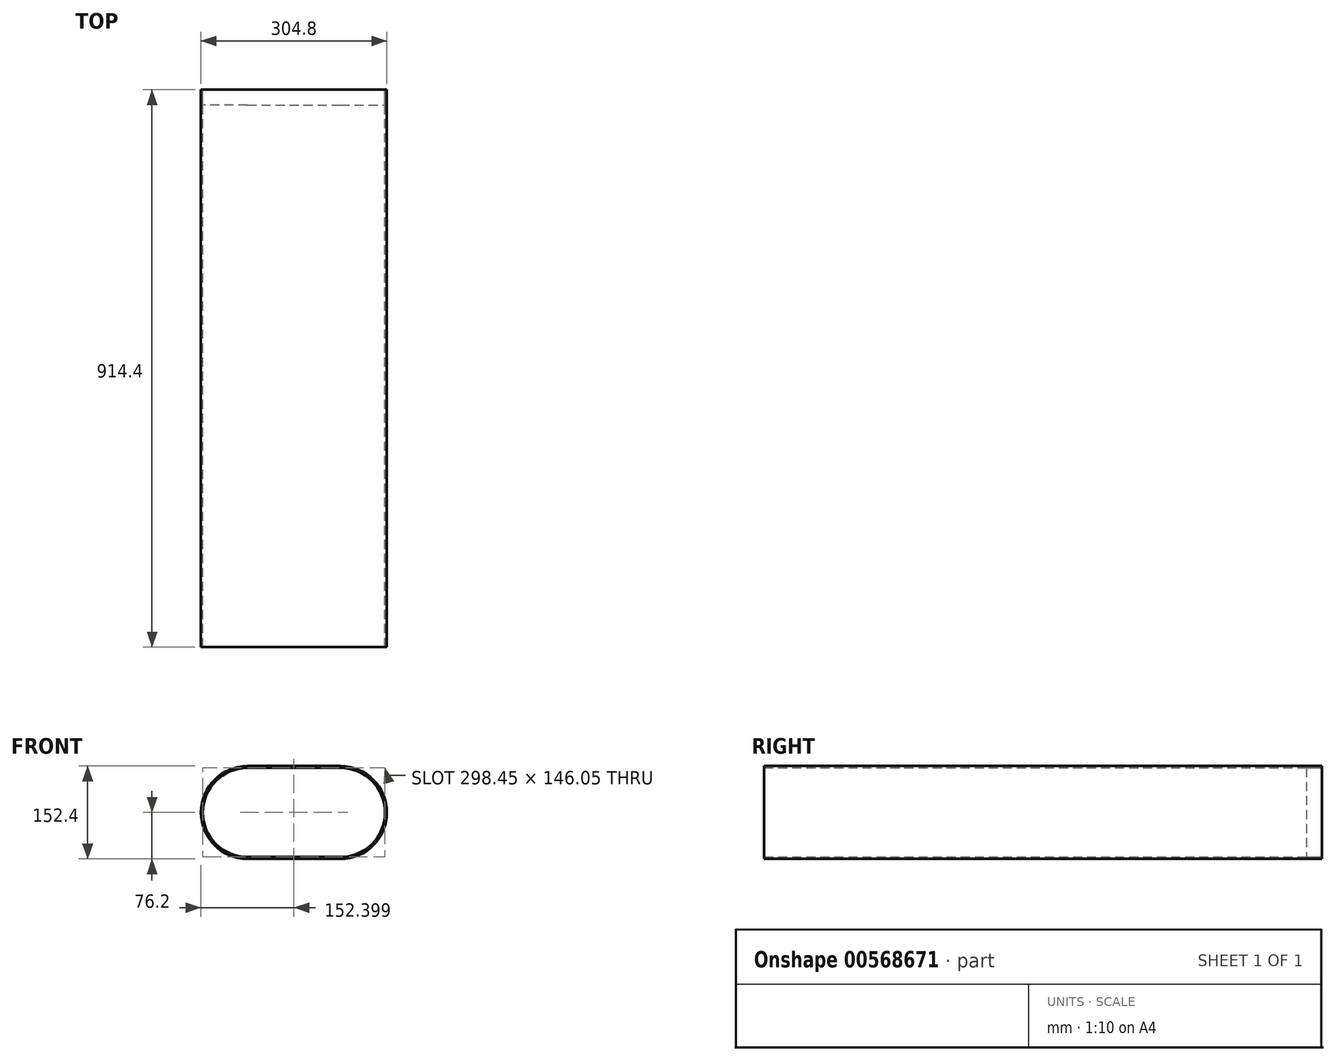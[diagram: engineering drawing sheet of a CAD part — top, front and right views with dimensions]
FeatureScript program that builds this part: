
annotation { "Feature Type Name" : "Feature", "Feature Type Description" : "" }
export const myFeature = defineFeature(function(context is Context, id is Id, definition is map)
    precondition{}
    {
        {
            var Q0;
            Q0=qCreatedBy(makeId("Front.planeOp"),FACE);
            var sketch = newSketch(context, id + "F0", { "sketchPlane" : qUnion([Q0])});
            skArc(sketch, "E0", {"start": v(-116.1, 76.2) * mm, "mid": v(-192.3, 0) * mm, "end": v(-116.1, -76.2) * mm});
            skArc(sketch, "E1", {"start": v(36.3, -76.2) * mm, "mid": v(112.5, 0) * mm, "end": v(36.3, 76.2) * mm});
            skArc(sketch, "E2", {"start": v(-116.1, 73.03) * mm, "mid": v(-189.13, 0) * mm, "end": v(-116.1, -73.03) * mm});
            skArc(sketch, "E3", {"start": v(36.3, -73.03) * mm, "mid": v(109.32, 0) * mm, "end": v(36.3, 73.02) * mm});
            skLineSegment(sketch, "E4", {"start": v(-116.1, 76.2) * mm, "end": v(36.3, 76.2) * mm});
            skLineSegment(sketch, "E5", {"start": v(-116.1, 73.03) * mm, "end": v(36.3, 73.02) * mm});
            skLineSegment(sketch, "E6", {"start": v(-116.1, -73.03) * mm, "end": v(36.3, -73.03) * mm});
            skLineSegment(sketch, "E7", {"start": v(-116.1, -76.2) * mm, "end": v(36.3, -76.2) * mm});
            skSolve(sketch);
        }
        {
            var Q0;
            Q0 = qSketchRegion(id + "F0", true);
            extrude(context, id + "F1", {"entities" : qUnion([Q0]), "depth" : 914.4 * mm, "offsetDistance" : 25.4 * mm});
        }
        {
            var Q0;
            Q0=makeQuery(id+"F0.imprint","IMPRINT",FACE,{"disambiguationData":[TD([[makeQuery(id+"F0.imprint","IMPRINT",EDGE,{"derivedFrom":sQuery(id+"F0.wireOp",EDGE,"E2")}),1.0]])]});
            extrude(context, id + "F2", {"entities" : qUnion([Q0]), "depth" : 25.4 * mm, "offsetDistance" : 25.4 * mm});
        }
    });
